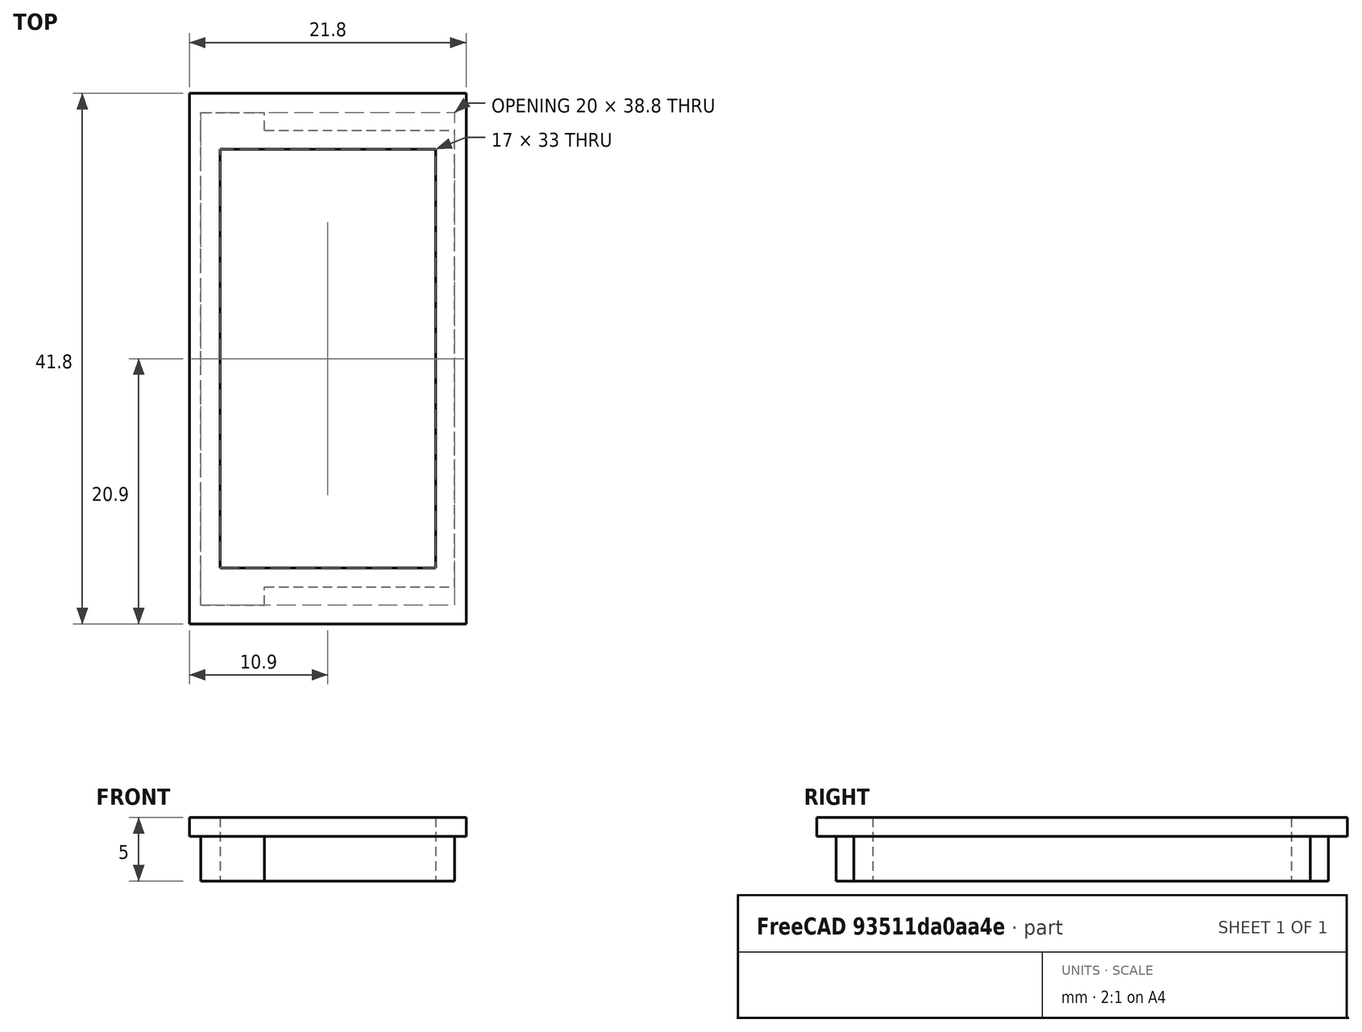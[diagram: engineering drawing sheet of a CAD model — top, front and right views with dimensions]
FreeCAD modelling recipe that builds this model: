
FCSTD DOCUMENT  (FreeCAD 0.17R13522 (Git))
Label: BaseUpperSensorMount
License: All rights reserved
LicenseURL: http://en.wikipedia.org/wiki/All_rights_reserved
objects: Part::Box×5, Part::MultiFuse×3, Part::Cut×1
note: 9 computed .brp shape members not serialized (recipe doc carries the construction recipe); baked Part::Feature solids carry a one-line shape summary decoded from their .brp

FEATURE [Part::Box] Box003  label="Cube001"
  AttacherType = Attacher::AttachEngine3D
  Height = 5
  Length = 5
  Placement = pos=(-10,17.4,0) rot=(0,0,1;0rad)
  Width = 2
FEATURE [Part::Box] Box005  label="Cube003"
  AttacherType = Attacher::AttachEngine3D
  Height = 5
  Length = 5
  Placement = pos=(-10,-19.4,0) rot=(0,0,1;0rad)
  Width = 2
FEATURE [Part::MultiFuse] Fusion003
  Placement = pos=(15,0,0) rot=(0,0,1;0rad)
  Shapes = -> [Box005,Box003]
FEATURE [Part::Box] Box  label="outer base"
  AttacherType = Attacher::AttachEngine3D
  Height = 1.5
  Length = 21.8
  Placement = pos=(-10.9,-20.9,0) rot=(0,0,1;0rad)
  Width = 41.8
FEATURE [Part::Box] Box001  label="Cube"
  AttacherType = Attacher::AttachEngine3D
  Height = 5
  Length = 20
  Placement = pos=(-10,-18,0) rot=(0,0,1;0rad)
  Width = 36
FEATURE [Part::MultiFuse] Fusion
  Shapes = -> [Box,Box001]
FEATURE [Part::Box] Box002  label="cut"
  AttacherType = Attacher::AttachEngine3D
  Height = 5
  Length = 17
  Placement = pos=(-8.5,-16.5,0) rot=(0,0,1;0rad)
  Width = 33
FEATURE [Part::Cut] Cut  label="Base"
  Base = -> Fusion
  Tool = -> Box002
FEATURE [Part::MultiFuse] Fusion004  label="BaseSensorUpperMount"
  Placement = pos=(0,0,1.5) rot=(0,1,0;3.14159rad)
  Shapes = -> [Cut,Fusion003]
